# Revit family: Faucet-Kitchen-KOHLER-Taut-K-21367K
name_source: partatom
category: Plumbing Fixtures
units: mm (PartAtom-declared; Revit-internal decimal feet)

## family parameters
Cut with Voids When Loaded = No
Host = Face
OmniClass Number = 23.31.11.00
OmniClass Title = Faucets
Part Type = Normal
Room Calculation Point = No
Round Connector Dimension = Use Diameter
Shared = No

## types (3) — shared parameters
ADA Compliant = No
Assembly Code = D2010
CW Connection = Yes
Cold Water Inlet = Cold Water Inlet
Date Modified = 04/20/2023
Default Elevation = 36"
Description = Pull Down Kitchen Faucet
Drain Included = No
Flow Rate = 2 GPM
HW Connection = Yes
Handle Clearance = 3 1/8"
Height = 15 5/16"
Hot Water Inlet = Hot Water Inlet
Length = 8 3/4"
Manufacturer = Kohler Co.
Master Format 2014 = 22 41 39
Master Format 2014 Name = Residential Faucets, Supplies, and Trim
Material = Premium Metal Construction
Model = Taut
Pressure = 60.00 psi
Product Documentation Link = https://resources.kohler.com
Spout Reach = 8 3/4"
URL = https://www.kohlerasiapacific.com
Vent Connection = No
Waste Connection = No
Waste Water Outlet = Waste Water Outlet
WaterSense Certified = No
Width = 2"

## per-type parameters (varying)
| type | Finish | Product Name | Product Page URL | Type |
| BL-Matte Black | Kohler-Metal-BL-Matte_Black | K-21367K-4-BL | https://www.kohlerasiapacific.com | 1 |
| CP-Polished Chrome | Kohler-Metal-CP-Polished_Chrome | K-21367K-4-CP |  | 2 |
| VS-Vibrant Stainless | Kohler-Metal-VS-Vibrant_Stainless | K-21367K-4-VS |  | 3 |

## geometry (parser evidence)
native form markers: Sweep x5
no freeform markers — native parametric forms only
